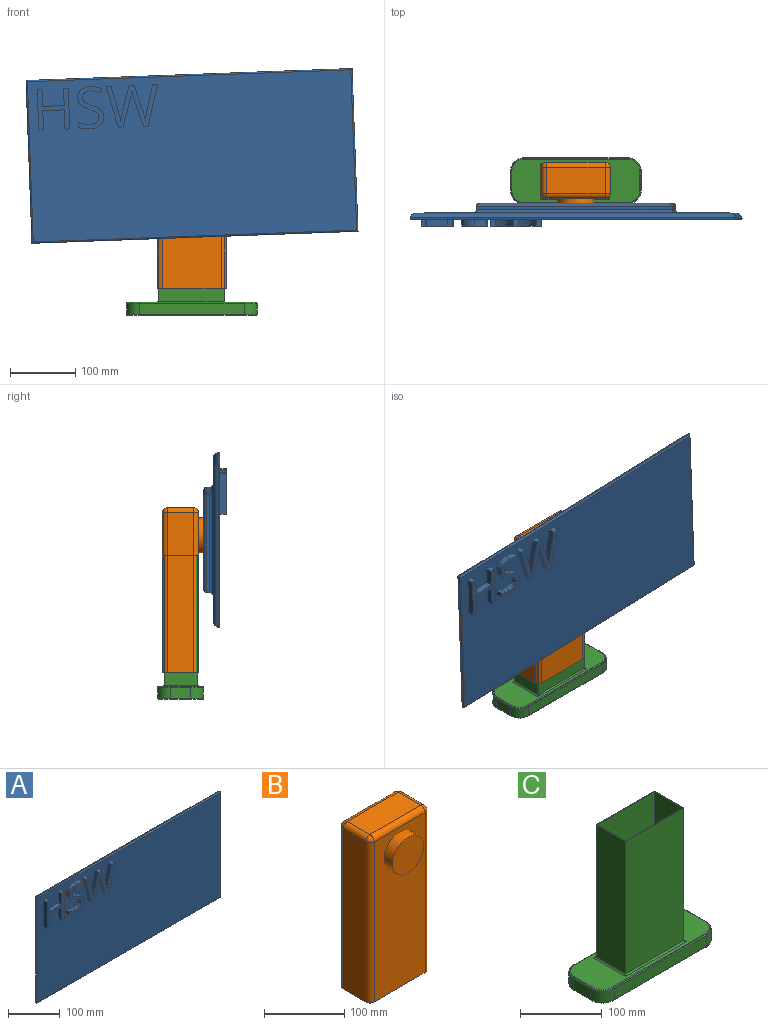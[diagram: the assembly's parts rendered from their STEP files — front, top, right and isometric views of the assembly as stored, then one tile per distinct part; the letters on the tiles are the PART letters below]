
ASSEMBLY  parts=3 mates=2
PART A: 85 faces, bbox 499.5x35x249.5 mm
  f0: plane 495.49x245.49mm, normal (0,-1,0), area 117932mm2, adj f13,f14,f15,f16,f17,f18,f19,f20
  f1: plane 480x230mm, normal (0,1,0), area 60800mm2, adj f7,f8,f9,f10,f77,f78,f79,f80
  f2: plane 150x5mm, normal (1,0,0), area 750mm2, adj f3,f5,f77,f81
  f3: plane 300x5mm, normal (0,0,-1), area 1500mm2, adj f2,f4,f79,f83
  f4: plane 150x5mm, normal (-1,0,0), area 750mm2, adj f3,f5,f80,f84
  f5: plane 300x5mm, normal (0,0,1), area 1500mm2, adj f2,f4,f78,f82
  f6: plane 290x140mm, normal (0,1,0), area 38636.5mm2, adj f11,f81,f82,f83,f84
  f7: cylinder r=10mm len=499.37mm, axis (-1,0,0), area 6477mm2, adj f1,f8,f9,f13
  f8: cylinder r=10mm len=249.37mm, axis (0,0,-1), area 3181.7mm2, adj f1,f7,f10,f14
  f9: cylinder r=10mm len=249.37mm, axis (0,0,1), area 3181.7mm2, adj f1,f7,f10,f15
  f10: cylinder r=10mm len=499.37mm, axis (1,0,0), area 6477mm2, adj f1,f8,f9,f16
  f11: cylinder r=25mm len=50mm, axis (0,1,0), area 1570.8mm2, adj f6,f12
  f12: plane 50x50mm, normal (0,1,0), area 1963.5mm2, adj f11
  f13: cylinder r=2mm len=499.5mm, axis (-1,0,0), area 1817mm2, adj f0,f7,f14,f15
  f14: cylinder r=2mm len=249.5mm, axis (0,0,-1), area 905.3mm2, adj f0,f8,f13,f16
  f15: cylinder r=2mm len=249.5mm, axis (0,0,1), area 905.3mm2, adj f0,f9,f13,f16
  f16: cylinder r=2mm len=499.5mm, axis (1,0,0), area 1817mm2, adj f0,f10,f14,f15
  f17: plane 62.63x10mm, normal (1,0,0), area 626.3mm2, adj f0,f18,f26,f27
  f18: plane 10x7.28mm, normal (0,0,1), area 72.8mm2, adj f0,f17,f19,f26
  f19: plane 26.65x10mm, normal (-1,0,0), area 266.5mm2, adj f0,f18,f20,f26
  f20: plane 32.99x10mm, normal (0,0,1), area 329.9mm2, adj f0,f19,f21,f26
  f21: plane 26.65x10mm, normal (1,0,0), area 266.5mm2, adj f0,f20,f22,f26
  f22: plane 10x7.28mm, normal (0,0,1), area 72.8mm2, adj f0,f21,f23,f26
  f23: plane 62.63x10mm, normal (-1,0,0), area 626.3mm2, adj f0,f22,f24,f26
  f24: plane 10x7.28mm, normal (0,0,-1), area 72.8mm2, adj f0,f23,f25,f26
  f25: plane 29.47x10mm, normal (1,0,0), area 294.7mm2, adj f0,f24,f26,f28
  f26: plane 62.63x47.55mm, normal (0,-1,0), area 1126.6mm2, adj f17,f18,f19,f20,f21,f22,f23,f24
  f27: plane 10x7.28mm, normal (0,0,-1), area 72.8mm2, adj f0,f17,f26,f29
  f28: plane 32.99x10mm, normal (0,0,-1), area 329.9mm2, adj f0,f25,f26,f29
  f29: plane 29.47x10mm, normal (-1,0,0), area 294.7mm2, adj f0,f26,f27,f28
  f30: extruded ~10.45x10mm, area 113.5mm2, adj f0,f31,f52,f53
  f31: extruded ~13.56x10mm, area 156.5mm2, adj f0,f30,f32,f52
  f32: extruded ~10x8.72mm, area 95.4mm2, adj f0,f31,f33,f52
  f33: extruded ~10x4.05mm, area 56.2mm2, adj f0,f32,f34,f52
  f34: extruded ~10x5.33mm, area 55.3mm2, adj f0,f33,f35,f52
  f35: extruded ~10x6.9mm, area 79.3mm2, adj f0,f34,f36,f52
  f36: extruded ~10x9.04mm, area 95.4mm2, adj f0,f35,f37,f52
  f37: extruded ~15.08x10mm, area 155.3mm2, adj f0,f36,f38,f52
  f38: plane 10x6.33mm, normal (0.94,0,-0.34), area 67.3mm2, adj f0,f37,f39,f52
  f39: extruded ~17.18x10mm, area 176.4mm2, adj f0,f38,f40,f52
  f40: extruded ~14.4x10mm, area 153.1mm2, adj f0,f39,f41,f52
  f41: extruded ~11.52x10mm, area 132.2mm2, adj f0,f40,f42,f52
  f42: extruded ~11.18x10mm, area 120.6mm2, adj f0,f41,f43,f52
  f43: extruded ~12.48x10mm, area 146.6mm2, adj f0,f42,f44,f52
  f44: extruded ~10x9.31mm, area 101.4mm2, adj f0,f43,f45,f52
  f45: extruded ~10x4.37mm, area 58.7mm2, adj f0,f44,f46,f52
  f46: extruded ~10x5.33mm, area 55.6mm2, adj f0,f45,f47,f52
  f47: extruded ~10x7.7mm, area 88.8mm2, adj f0,f46,f48,f52
  f48: extruded ~10.97x10mm, area 115mm2, adj f0,f47,f49,f52
  f49: extruded ~10x8.99mm, area 90.6mm2, adj f0,f48,f50,f52
  f50: extruded ~10x8.4mm, area 88mm2, adj f0,f49,f51,f52
  f51: plane 10x7.02mm, normal (-1,0,0), area 70.2mm2, adj f0,f50,f52,f54
  f52: plane 64.38x39.41mm, normal (0,-1,0), area 907.9mm2, adj f30,f31,f32,f33,f34,f35,f36,f37
  f53: extruded ~12.9x10mm, area 147.8mm2, adj f0,f30,f52,f55
  f54: extruded ~17.13x10mm, area 175.1mm2, adj f0,f51,f52,f55
  f55: extruded ~16.28x10mm, area 172.4mm2, adj f0,f52,f53,f54
  f56: plane 62.63x16.75mm, normal (0.97,0,-0.26), area 648.3mm2, adj f0,f57,f73,f74
  f57: plane 10x7.72mm, normal (0,0,1), area 77.2mm2, adj f0,f56,f58,f73
  f58: plane 38.6x10mm, normal (-0.97,0,0.25), area 398.4mm2, adj f0,f57,f59,f73
  f59: extruded ~14.82x10mm, area 151.4mm2, adj f0,f58,f60,f73
  f60: extruded ~15x10mm, area 154mm2, adj f0,f59,f61,f73
  f61: plane 38.42x11.77mm, normal (0.96,0,0.29), area 401.9mm2, adj f0,f60,f62,f73
  f62: plane 10x7.72mm, normal (0,0,1), area 77.2mm2, adj f0,f61,f63,f73
  f63: plane 38.08x11.21mm, normal (-0.96,0,0.28), area 397mm2, adj f0,f62,f64,f73
  f64: extruded ~15.34x10mm, area 157.3mm2, adj f0,f63,f65,f73
  f65: extruded ~14.74x10mm, area 150.5mm2, adj f0,f64,f66,f73
  f66: plane 38.68x10mm, normal (0.97,0,0.25), area 399.3mm2, adj f0,f65,f67,f73
  f67: plane 10x7.72mm, normal (0,0,1), area 77.2mm2, adj f0,f66,f68,f73
  f68: plane 62.63x16.67mm, normal (-0.97,0,-0.26), area 648.1mm2, adj f0,f67,f69,f73
  f69: plane 10x7.2mm, normal (0,0,-1), area 72mm2, adj f0,f68,f70,f73
  f70: plane 41.68x12.25mm, normal (0.96,0,-0.28), area 434.5mm2, adj f0,f69,f71,f73
  f71: extruded ~12.38x10mm, area 127.5mm2, adj f0,f70,f72,f73
  f72: extruded ~10x5.1mm, area 52.3mm2, adj f0,f71,f73,f75
  f73: plane 78.87x62.63mm, normal (0,-1,0), area 1672.9mm2, adj f56,f57,f58,f59,f60,f61,f62,f63
  f74: plane 10x7.2mm, normal (0,0,-1), area 72mm2, adj f0,f56,f73,f76
  f75: extruded ~10x7.03mm, area 73.2mm2, adj f0,f72,f73,f76
  f76: plane 41.93x12.64mm, normal (-0.96,0,-0.29), area 437.9mm2, adj f0,f73,f74,f75
  f77: cylinder r=5mm len=160mm, axis (0,0,1), area 1206.6mm2, adj f1,f2,f78,f79
  f78: cylinder r=5mm len=310mm, axis (-1,0,0), area 2384.7mm2, adj f1,f5,f77,f80
  f79: cylinder r=5mm len=310mm, axis (1,0,0), area 2384.7mm2, adj f1,f3,f77,f80
  f80: cylinder r=5mm len=160mm, axis (0,0,-1), area 1206.6mm2, adj f1,f4,f78,f79
  f81: cylinder r=5mm len=150mm, axis (0,0,1), area 1149.6mm2, adj f2,f6,f82,f83
  f82: cylinder r=5mm len=300mm, axis (-1,0,0), area 2327.7mm2, adj f5,f6,f81,f84
  f83: cylinder r=5mm len=300mm, axis (1,0,0), area 2327.7mm2, adj f3,f6,f81,f84
  f84: cylinder r=5mm len=150mm, axis (0,0,-1), area 1149.6mm2, adj f4,f6,f82,f83
PART B: 39 faces, bbox 105x70x252.5 mm
  f0: plane 105x55mm, normal (0,0,-1), area 748.2mm2, adj f1,f2,f3,f4,f8,f10,f13,f19
  f1: plane 245x90mm, normal (0,1,0), area 22050mm2, adj f0,f10,f16,f19
  f2: plane 245x40mm, normal (-1,0,0), area 9800mm2, adj f0,f13,f17,f19
  f3: plane 245x90mm, normal (0,-1,0), area 19674.2mm2, adj f0,f6,f8,f12,f13
  f4: plane 245x40mm, normal (1,0,0), area 9800mm2, adj f0,f8,f10,f11
  f5: plane 90x40mm, normal (0,0,1), area 3600mm2, adj f11,f12,f16,f17
  f6: cylinder r=27.5mm len=55mm, axis (0,1,0), area 2591.8mm2, adj f3,f7
  f7: plane 55x55mm, normal (0,-1,0), area 2375.8mm2, adj f6
  f8: cylinder r=7.5mm len=245mm, axis (0,0,1), area 2886.3mm2, adj f0,f3,f4,f9
  f9: sphere r=7.5mm, area 88.4mm2, adj f8,f11,f12
  f10: cylinder r=7.5mm len=245mm, axis (0,0,-1), area 2886.3mm2, adj f0,f1,f4,f14
  f11: cylinder r=7.5mm len=40mm, axis (0,-1,0), area 471.2mm2, adj f4,f5,f9,f14
  f12: cylinder r=7.5mm len=90mm, axis (-1,0,0), area 1060.3mm2, adj f3,f5,f9,f15
  f13: cylinder r=7.5mm len=245mm, axis (0,0,-1), area 2886.3mm2, adj f0,f2,f3,f15
  f14: sphere r=7.5mm, area 88.4mm2, adj f10,f11,f16
  f15: sphere r=7.5mm, area 88.4mm2, adj f12,f13,f17
  f16: cylinder r=7.5mm len=90mm, axis (1,0,0), area 1060.3mm2, adj f1,f5,f14,f18
  f17: cylinder r=7.5mm len=40mm, axis (0,1,0), area 471.2mm2, adj f2,f5,f15,f18
  f18: sphere r=7.5mm, area 88.4mm2, adj f16,f17,f19
  f19: cylinder r=7.5mm len=245mm, axis (0,0,1), area 2886.3mm2, adj f0,f1,f2,f18
  f20: plane 245x90mm, normal (0,-1,0), area 22050mm2, adj f0,f29,f35,f38
  f21: plane 245x40mm, normal (1,0,0), area 9800mm2, adj f0,f32,f36,f38
  f22: plane 245x90mm, normal (0,1,0), area 20086.5mm2, adj f0,f25,f27,f31,f32
  f23: plane 245x40mm, normal (-1,0,0), area 9800mm2, adj f0,f27,f29,f30
  f24: plane 90x40mm, normal (0,0,-1), area 3600mm2, adj f30,f31,f35,f36
  f25: cylinder r=25mm len=50mm, axis (0,1,0), area 2356.2mm2, adj f22,f26
  f26: plane 50x50mm, normal (0,1,0), area 1963.5mm2, adj f25
  f27: cylinder r=5mm len=245mm, axis (0,0,1), area 1924.2mm2, adj f0,f22,f23,f28
  f28: sphere r=5mm, area 39.3mm2, adj f27,f30,f31
  f29: cylinder r=5mm len=245mm, axis (0,0,-1), area 1924.2mm2, adj f0,f20,f23,f33
  f30: cylinder r=5mm len=40mm, axis (0,-1,0), area 314.2mm2, adj f23,f24,f28,f33
  f31: cylinder r=5mm len=90mm, axis (-1,0,0), area 706.9mm2, adj f22,f24,f28,f34
  f32: cylinder r=5mm len=245mm, axis (0,0,-1), area 1924.2mm2, adj f0,f21,f22,f34
  f33: sphere r=5mm, area 39.3mm2, adj f29,f30,f35
  f34: sphere r=5mm, area 39.3mm2, adj f31,f32,f36
  f35: cylinder r=5mm len=90mm, axis (1,0,0), area 706.9mm2, adj f20,f24,f33,f37
  f36: cylinder r=5mm len=40mm, axis (0,1,0), area 314.2mm2, adj f21,f24,f34,f37
  f37: sphere r=5mm, area 39.3mm2, adj f35,f36,f38
  f38: cylinder r=5mm len=245mm, axis (0,0,1), area 1924.2mm2, adj f0,f20,f21,f37
PART C: 57 faces, bbox 203.3x73.3x220 mm
  f0: plane 160x16mm, normal (0,1,0), area 2560mm2, adj f1,f7,f31,f44
  f1: cylinder r=20mm len=20mm, axis (0,0,-1), area 502.7mm2, adj f0,f2,f29,f42
  f2: plane 30x16mm, normal (-1,0,0), area 480mm2, adj f1,f3,f30,f41
  f3: cylinder r=20mm len=20mm, axis (0,0,-1), area 502.7mm2, adj f2,f4,f32,f43
  f4: plane 160x16mm, normal (0,-1,0), area 2560mm2, adj f3,f5,f34,f45
  f5: cylinder r=20mm len=20mm, axis (0,0,-1), area 502.7mm2, adj f4,f6,f36,f47
  f6: plane 30x16mm, normal (1,0,0), area 480mm2, adj f5,f7,f35,f48
  f7: cylinder r=20mm len=20mm, axis (0,0,-1), area 502.7mm2, adj f0,f6,f33,f46
  f8: plane 196x66mm, normal (0,0,1), area 6802.6mm2, adj f37,f38,f39,f40,f41,f42,f43,f44
  f9: plane 196x66mm, normal (0,0,-1), area 12657.9mm2, adj f29,f30,f31,f32,f33,f34,f35,f36
  f10: plane 198x50.5mm, normal (-1,0,0), area 9999mm2, adj f14,f37,f49,f55
  f11: plane 198x100.5mm, normal (0,-1,0), area 19899mm2, adj f14,f39,f49,f51
  f12: plane 198x50.5mm, normal (1,0,0), area 9999mm2, adj f14,f40,f51,f53
  f13: plane 198x100.5mm, normal (0,1,0), area 19899mm2, adj f14,f38,f53,f55
  f14: plane 101.5x51.5mm, normal (0,0,1), area 301.8mm2, adj f10,f11,f12,f13,f25,f26,f27,f28
  f15: plane 160x18mm, normal (0,-1,0), area 2880mm2, adj f16,f22,f23,f24
  f16: cylinder r=19mm len=19mm, axis (0,0,-1), area 537.2mm2, adj f15,f17,f23,f24
  f17: plane 30x18mm, normal (1,0,0), area 540mm2, adj f16,f18,f23,f24
  f18: cylinder r=19mm len=19mm, axis (0,0,-1), area 537.2mm2, adj f17,f19,f23,f24
  f19: plane 160x18mm, normal (0,1,0), area 2880mm2, adj f18,f20,f23,f24
  f20: cylinder r=19mm len=19mm, axis (0,0,-1), area 537.2mm2, adj f19,f21,f23,f24
  f21: plane 30x18mm, normal (-1,0,0), area 540mm2, adj f20,f22,f23,f24
  f22: cylinder r=19mm len=19mm, axis (0,0,-1), area 537.2mm2, adj f15,f21,f23,f24
  f23: plane 198x68mm, normal (0,0,-1), area 8228.9mm2, adj f15,f16,f17,f18,f19,f20,f21,f22
  f24: plane 198x68mm, normal (0,0,1), area 13154.1mm2, adj f15,f16,f17,f18,f19,f20,f21,f22
  f25: plane 201x49.5mm, normal (1,0,0), area 9949.5mm2, adj f14,f23,f26,f28
  f26: plane 201x99.5mm, normal (0,1,0), area 19999.5mm2, adj f14,f23,f25,f27
  f27: plane 201x49.5mm, normal (-1,0,0), area 9949.5mm2, adj f14,f23,f26,f28
  f28: plane 201x99.5mm, normal (0,-1,0), area 19999.5mm2, adj f14,f23,f25,f27
  f29: torus R=18mm, axis (0,0,1), area 95.1mm2, adj f1,f9,f30,f31
  f30: cylinder r=2mm len=30mm, axis (0,-1,0), area 94.2mm2, adj f2,f9,f29,f32
  f31: cylinder r=2mm len=160mm, axis (-1,0,0), area 502.7mm2, adj f0,f9,f29,f33
  f32: torus R=18mm, axis (0,0,1), area 95.1mm2, adj f3,f9,f30,f34
  f33: torus R=18mm, axis (0,0,1), area 95.1mm2, adj f7,f9,f31,f35
  f34: cylinder r=2mm len=160mm, axis (1,0,0), area 502.7mm2, adj f4,f9,f32,f36
  f35: cylinder r=2mm len=30mm, axis (0,1,0), area 94.2mm2, adj f6,f9,f33,f36
  f36: torus R=18mm, axis (0,0,1), area 95.1mm2, adj f5,f9,f34,f35
  f37: cylinder r=2mm len=55.5mm, axis (0,-1,0), area 164.4mm2, adj f8,f10,f50,f56
  f38: cylinder r=2mm len=105.5mm, axis (-1,0,0), area 321.4mm2, adj f8,f13,f54,f56
  f39: cylinder r=2mm len=105.5mm, axis (1,0,0), area 321.4mm2, adj f8,f11,f50,f52
  f40: cylinder r=2mm len=55.5mm, axis (0,1,0), area 164.4mm2, adj f8,f12,f52,f54
  f41: cylinder r=2mm len=30mm, axis (0,1,0), area 94.2mm2, adj f2,f8,f42,f43
  f42: torus R=18mm, axis (0,0,1), area 95.1mm2, adj f1,f8,f41,f44
  f43: torus R=18mm, axis (0,0,1), area 95.1mm2, adj f3,f8,f41,f45
  f44: cylinder r=2mm len=160mm, axis (1,0,0), area 502.7mm2, adj f0,f8,f42,f46
  f45: cylinder r=2mm len=160mm, axis (-1,0,0), area 502.7mm2, adj f4,f8,f43,f47
  f46: torus R=18mm, axis (0,0,1), area 95.1mm2, adj f7,f8,f44,f48
  f47: torus R=18mm, axis (0,0,1), area 95.1mm2, adj f5,f8,f45,f48
  f48: cylinder r=2mm len=30mm, axis (0,-1,0), area 94.2mm2, adj f6,f8,f46,f47
  f49: cylinder r=0.5mm len=198mm, axis (0,0,-1), area 155.5mm2, adj f10,f11,f14,f50
  f50: bspline ~2.5x2.5mm, area 1.8mm2, adj f37,f39,f49
  f51: cylinder r=0.5mm len=198mm, axis (0,0,1), area 155.5mm2, adj f11,f12,f14,f52
  f52: bspline ~2.5x2.5mm, area 1.8mm2, adj f39,f40,f51
  f53: cylinder r=0.5mm len=198mm, axis (0,0,-1), area 155.5mm2, adj f12,f13,f14,f54
  f54: bspline ~2.5x2.5mm, area 1.8mm2, adj f38,f40,f53
  f55: cylinder r=0.5mm len=198mm, axis (0,0,1), area 155.5mm2, adj f10,f13,f14,f56
  f56: bspline ~2.5x2.5mm, area 1.8mm2, adj f37,f38,f55
PLACE A rot(axis=(0,-1,0),2.1deg) t=(0.24,-50,244.34)mm
PLACE B t=(0,0,41)mm
PLACE C at identity fixed
MATE slider C.f24 <-> B.f0  axis (0,0,1) through (0,0,1)mm
MATE revolute B.f6 <-> A.f11  axis (0,1,0) through (0,-35,251)mm
